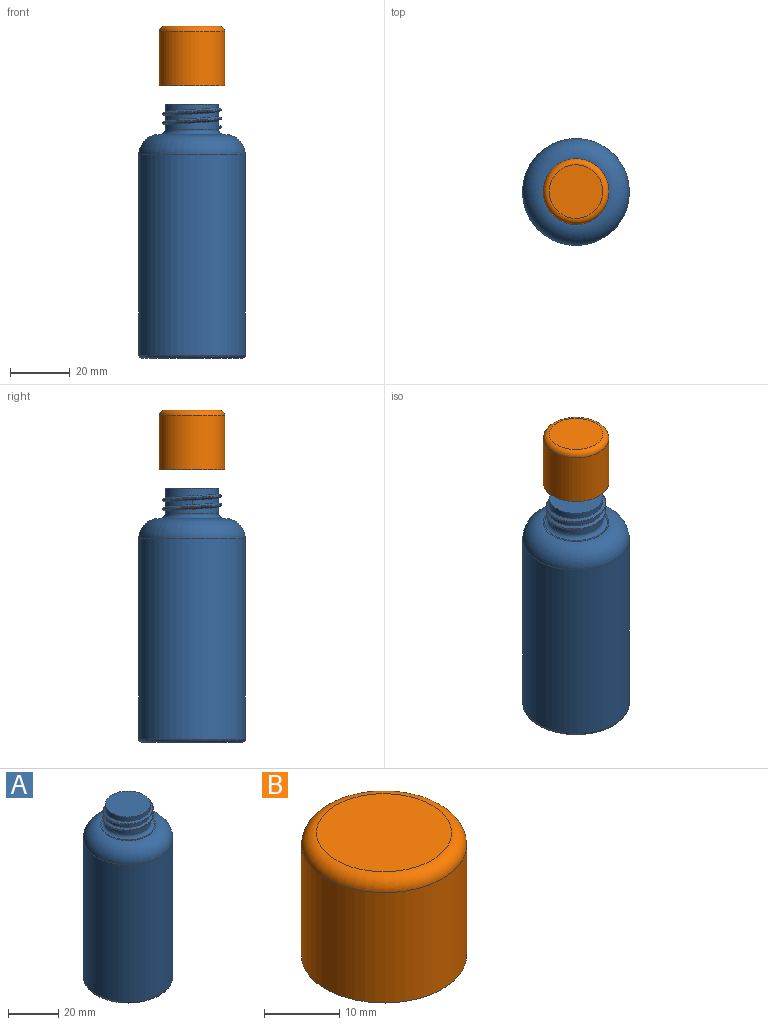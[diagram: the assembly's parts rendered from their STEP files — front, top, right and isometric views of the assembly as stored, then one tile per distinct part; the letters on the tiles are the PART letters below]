
ASSEMBLY  parts=2 mates=1
PART A: 32 faces, bbox 38.7x38.7x85.1 mm
  f0: cylinder r=9mm len=18mm, axis (0,0,-1), area 130.3mm2, adj f1,f6,f7,f9,f10,f13,f17
  f1: cylinder r=9mm len=18mm, axis (0,0,-1), area 181.5mm2, adj f0,f5,f6,f7,f14,f15,f16
  f2: cylinder r=17.89mm len=67.11mm, axis (0,0,1), area 7542.6mm2, adj f3,f8
  f3: torus R=11mm, axis (0,0,1), area 1045.7mm2, adj f2,f4
  f4: plane 22x22mm, normal (0,0,1), area 33.8mm2, adj f3,f17
  f5: plane 18x18mm, normal (0,0,1), area 254.5mm2, adj f1
  f6: bspline ~23.56x20.4mm, area 130.3mm2, adj f0,f1,f10,f11,f14
  f7: bspline ~23.56x20.4mm, area 130.3mm2, adj f0,f1,f9,f11,f12,f16
  f8: torus R=16.89mm, axis (0,0,1), area 173mm2, adj f2,f18
  f9: cone r=2mm half-angle=58deg, axis (0,0,1), area 1.4mm2, adj f0,f7,f13
  f10: cone r=3.2mm half-angle=58deg, axis (0,0,-1), area 1.4mm2, adj f0,f6,f13
  f11: bspline ~20.41x20.4mm, area 50.9mm2, adj f6,f7,f12,f15
  f12: bspline ~2.09x0.42mm, area 0mm2, adj f7,f11,f13
  f13: torus R=2.82mm, axis (0,0,-1), area 1.2mm2, adj f0,f9,f10,f12
  f14: cone r=2.93mm half-angle=58deg, axis (0,0,-1), area 1.4mm2, adj f1,f6,f15
  f15: revolved ~2.54x1.44mm, area 1.2mm2, adj f1,f11,f14,f16
  f16: cone r=2mm half-angle=58deg, axis (0,0,1), area 1.4mm2, adj f1,f7,f15
  f17: torus R=10.5mm, axis (0,0,-1), area 141.3mm2, adj f0,f4
  f18: plane 33.77x33.77mm, normal (0,0,-1), area 895.9mm2, adj f8
  f19: plane 17x17mm, normal (0,0,1), area 227mm2, adj f25
  f20: cone r=1.74mm half-angle=58deg, axis (0,0,1), area 0.9mm2, adj f23,f25
  f21: cone r=1.74mm half-angle=58deg, axis (0,0,1), area 0.9mm2, adj f22,f24
  f22: cone r=2.94mm half-angle=58deg, axis (0,0,-1), area 1.2mm2, adj f21,f24
  f23: cone r=2.66mm half-angle=58deg, axis (0,0,-1), area 0.9mm2, adj f20,f25
  f24: cylinder r=8.5mm len=17mm, axis (0,0,-1), area 154mm2, adj f21,f22,f25,f26
  f25: cylinder r=8.5mm len=17mm, axis (0,0,-1), area 175.6mm2, adj f19,f20,f23,f24
  f26: torus R=10.5mm, axis (0,0,-1), area 182.1mm2, adj f24,f27
  f27: plane 22x22mm, normal (0,0,1), area 33.8mm2, adj f26,f28
  f28: torus R=11mm, axis (0,0,1), area 949.7mm2, adj f27,f29
  f29: cylinder r=17.39mm len=67.11mm, axis (0,0,1), area 7331.8mm2, adj f28,f30
  f30: torus R=16.89mm, axis (0,0,1), area 84.9mm2, adj f29,f31
  f31: plane 33.77x33.77mm, normal (0,0,-1), area 895.9mm2, adj f30
PART B: 7 faces, bbox 23.8x23.8x20 mm
  f0: cylinder r=11mm len=22mm, axis (0,0,-1), area 1244.1mm2, adj f2,f3
  f1: plane 18x18mm, normal (0,0,1), area 254.5mm2, adj f3
  f2: plane 22x22mm, normal (0,0,-1), area 96.6mm2, adj f0,f4
  f3: torus R=9mm, axis (0,0,1), area 202.8mm2, adj f0,f1
  f4: cylinder r=9.5mm len=19mm, axis (0,0,-1), area 1074.4mm2, adj f2,f6
  f5: plane 18x18mm, normal (0,0,-1), area 254.5mm2, adj f6
  f6: torus R=9mm, axis (0,0,1), area 46mm2, adj f4,f5
PLACE A t=(-13.57,-0.11,-42.99)mm
PLACE B t=(-13.57,-0.11,48.37)mm
MATE cylindrical B.f0 <-> A.f0  axis (0,0,-1) through (-13.57,-0.11,48.37)mm
